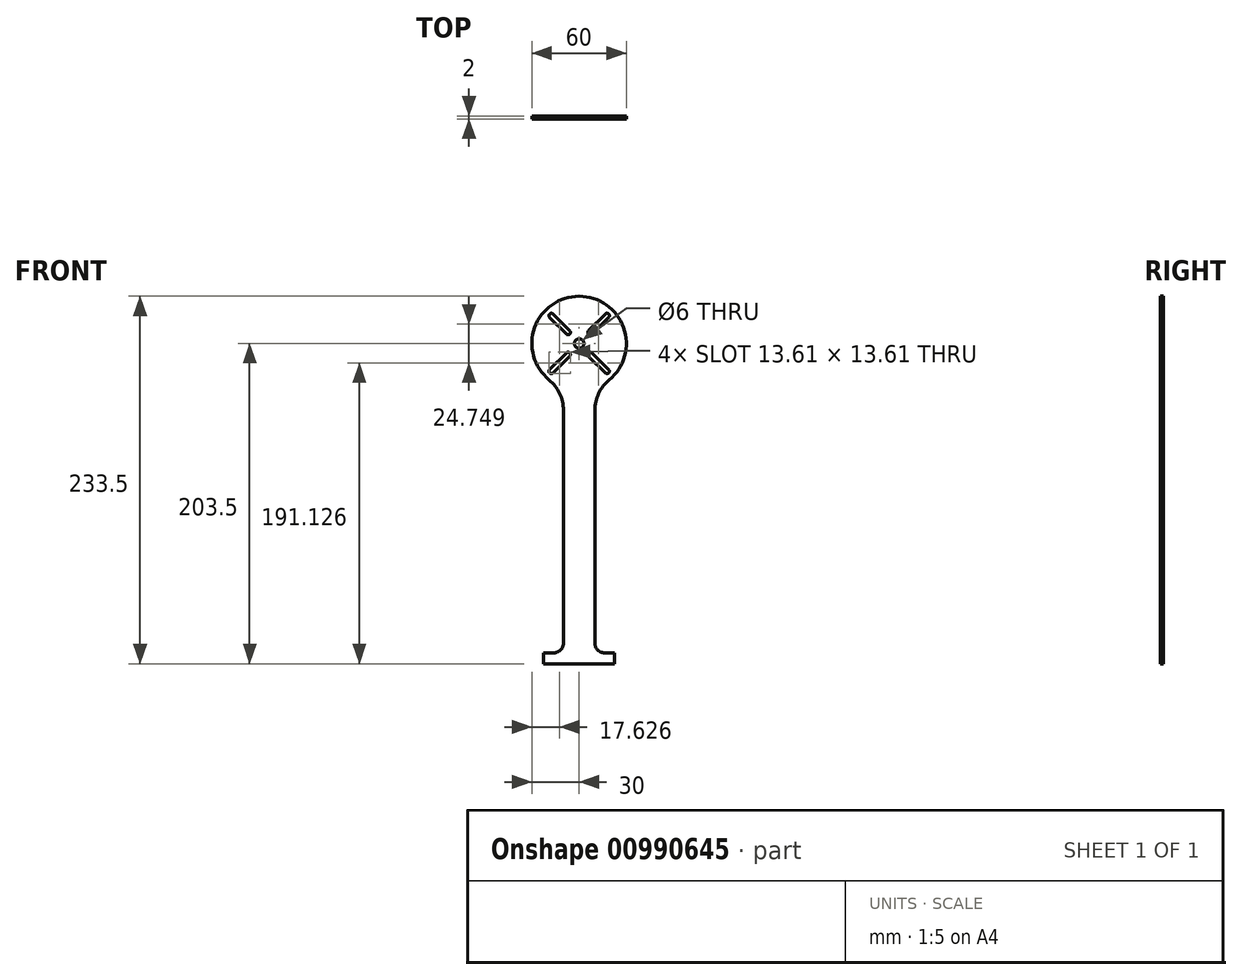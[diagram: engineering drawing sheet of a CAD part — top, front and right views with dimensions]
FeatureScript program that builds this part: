
annotation { "Feature Type Name" : "Feature", "Feature Type Description" : "" }
export const myFeature = defineFeature(function(context is Context, id is Id, definition is map)
    precondition{}
    {
        {
            var Q0;
            Q0=qCreatedBy(makeId("Front.planeOp"),FACE);
            var sketch = newSketch(context, id + "F0", { "sketchPlane" : qUnion([Q0])});
            skPoint(sketch, "E0.middle", {"position": v(0, 0) * mm});
            skArc(sketch, "E1", {"start": v(18.74, 16.62) * mm, "mid": v(18.74, 18.74) * mm, "end": v(16.62, 18.74) * mm});
            skArc(sketch, "E2", {"start": v(6.01, 8.13) * mm, "mid": v(6.01, 6.01) * mm, "end": v(8.13, 6.01) * mm});
            skLineSegment(sketch, "E3.trimOffspring", {"start": v(18.74, 16.62) * mm, "end": v(8.13, 6.01) * mm});
            skLineSegment(sketch, "E4.trimOffspring", {"start": v(16.62, 18.74) * mm, "end": v(6.01, 8.13) * mm});
            skLineSegment(sketch, "E5.MirrorCS", {"start": v(-16.62, 18.74) * mm, "end": v(-6.01, 8.13) * mm});
            skArc(sketch, "E6.MirrorCS", {"start": v(-18.74, 16.62) * mm, "mid": v(-18.74, 18.74) * mm, "end": v(-16.62, 18.74) * mm});
            skLineSegment(sketch, "E7.MirrorCS", {"start": v(-18.74, 16.62) * mm, "end": v(-8.13, 6.01) * mm});
            skArc(sketch, "E8.MirrorCS", {"start": v(-6.01, 8.13) * mm, "mid": v(-6.01, 6.01) * mm, "end": v(-8.13, 6.01) * mm});
            skLineSegment(sketch, "E9.MirrorCS", {"start": v(-16.62, -18.74) * mm, "end": v(-6.01, -8.13) * mm});
            skArc(sketch, "E10.MirrorCS", {"start": v(-18.74, -16.62) * mm, "mid": v(-18.74, -18.74) * mm, "end": v(-16.62, -18.74) * mm});
            skLineSegment(sketch, "E11.MirrorCS", {"start": v(-18.74, -16.62) * mm, "end": v(-8.13, -6.01) * mm});
            skArc(sketch, "E12.MirrorCS", {"start": v(-6.01, -8.13) * mm, "mid": v(-6.01, -6.01) * mm, "end": v(-8.13, -6.01) * mm});
            skArc(sketch, "E13.MirrorCS", {"start": v(18.74, -16.62) * mm, "mid": v(18.74, -18.74) * mm, "end": v(16.62, -18.74) * mm});
            skLineSegment(sketch, "E14.MirrorCS", {"start": v(16.62, -18.74) * mm, "end": v(6.01, -8.13) * mm});
            skLineSegment(sketch, "E15.MirrorCS", {"start": v(18.74, -16.62) * mm, "end": v(8.13, -6.01) * mm});
            skArc(sketch, "E16.MirrorCS", {"start": v(6.01, -8.13) * mm, "mid": v(6.01, -6.01) * mm, "end": v(8.13, -6.01) * mm});
            skCircle(sketch, "E17", {"center": v(0, 0) * mm, "radius": 3 * mm});
            skArc(sketch, "E18", {"start": v(19.1, -23.14) * mm, "mid": v(0, 30) * mm, "end": v(-19.1, -23.14) * mm});
            skLineSegment(sketch, "E19.trimOffspring", {"start": v(10, -42.43) * mm, "end": v(10, -190.5) * mm});
            skArc(sketch, "E20", {"start": v(19.1, -23.14) * mm, "mid": v(12.39, -31.77) * mm, "end": v(10, -42.43) * mm});
            skArc(sketch, "E21.MirrorCS", {"start": v(-19.1, -23.14) * mm, "mid": v(-12.39, -31.77) * mm, "end": v(-10, -42.43) * mm});
            skLineSegment(sketch, "E22.MirrorCS", {"start": v(-10, -42.43) * mm, "end": v(-10, -190.5) * mm});
            skLineSegment(sketch, "E23.bottom", {"start": v(-22.5, -203.5) * mm, "end": v(22.5, -203.5) * mm});
            skLineSegment(sketch, "E23.top", {"start": v(-22.5, -196.5) * mm, "end": v(-16, -196.5) * mm});
            skLineSegment(sketch, "E23.left", {"start": v(-22.5, -203.5) * mm, "end": v(-22.5, -196.5) * mm});
            skLineSegment(sketch, "E23.right", {"start": v(22.5, -203.5) * mm, "end": v(22.5, -196.5) * mm});
            skPoint(sketch, "E23.middle", {"position": v(0, -200) * mm});
            skArc(sketch, "E24", {"start": v(-16, -196.5) * mm, "mid": v(-11.76, -194.74) * mm, "end": v(-10, -190.5) * mm});
            skArc(sketch, "E25.MirrorCS", {"start": v(16, -196.5) * mm, "mid": v(11.76, -194.74) * mm, "end": v(10, -190.5) * mm});
            skLineSegment(sketch, "E26.trimOffspring", {"start": v(16, -196.5) * mm, "end": v(22.5, -196.5) * mm});
            skPoint(sketch, "E27.trimOffspring.end.orphan", {"position": v(-10, -200) * mm});
            skPoint(sketch, "E28.end.orphan", {"position": v(10, -200) * mm});
            skSolve(sketch);
        }
        {
            var Q0;
            Q0=makeQuery(id+"F0.imprint","IMPRINT",FACE,{"disambiguationData":[TD([[makeQuery(id+"F0.imprint","IMPRINT",EDGE,{"derivedFrom":sQuery(id+"F0.wireOp",EDGE,"E1")}),-1.0]])]});
            extrude(context, id + "F1", {"entities" : qUnion([Q0]), "depth" : 2 * mm, "offsetDistance" : 25 * mm});
        }
    });
